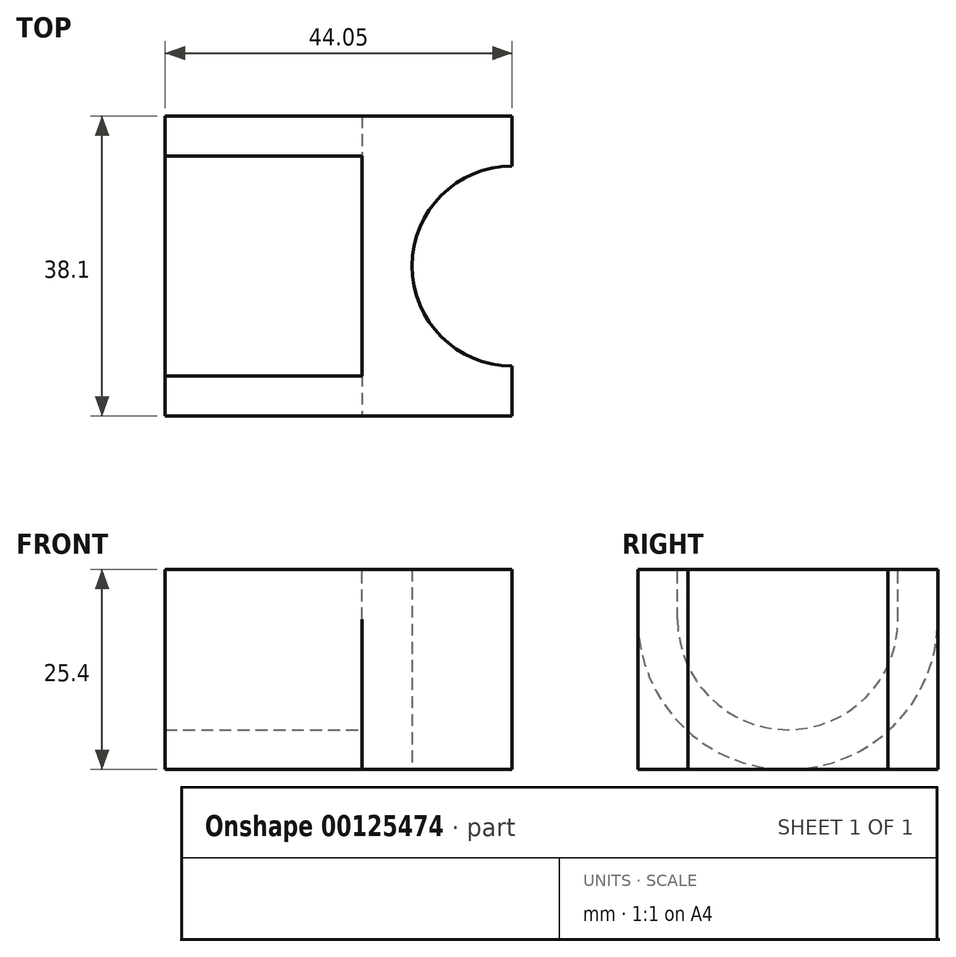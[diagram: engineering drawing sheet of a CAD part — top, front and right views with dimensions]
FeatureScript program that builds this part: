
annotation { "Feature Type Name" : "Feature", "Feature Type Description" : "" }
export const myFeature = defineFeature(function(context is Context, id is Id, definition is map)
    precondition{}
    {
        {
            var Q0;
            Q0=qCreatedBy(makeId("Top.planeOp"),FACE);
            var sketch = newSketch(context, id + "F0", { "sketchPlane" : qUnion([Q0])});
            skLineSegment(sketch, "E0.bottom", {"start": v(-6.35, 19.05) * mm, "end": v(12.7, 19.05) * mm});
            skLineSegment(sketch, "E0.top", {"start": v(-6.35, -19.05) * mm, "end": v(12.7, -19.05) * mm});
            skLineSegment(sketch, "E0.left", {"start": v(-6.35, 19.05) * mm, "end": v(-6.35, -19.05) * mm});
            skLineSegment(sketch, "E0.right", {"start": v(12.7, 19.05) * mm, "end": v(12.7, 12.7) * mm});
            skArc(sketch, "E1", {"start": v(12.7, 12.7) * mm, "mid": v(0, 0) * mm, "end": v(12.7, -12.7) * mm});
            skLineSegment(sketch, "E2.trimOffspring", {"start": v(12.7, -12.7) * mm, "end": v(12.7, -19.05) * mm});
            skSolve(sketch);
        }
        {
            var Q0;
            Q0 = qSketchRegion(id + "F0", true);
            extrude(context, id + "F1", {"entities" : qUnion([Q0]), "depth" : 25.4 * mm});
        }
        {
            var Q0;
            Q0=makeQuery(id+"F1.opExtrude","SWEPT_FACE",FACE,{"disambiguationData":[OSD([sQuery(id+"F0.wireOp",EDGE,"E0.left")])]});
            var sketch = newSketch(context, id + "F2", { "sketchPlane" : qUnion([Q0])});
            skArc(sketch, "E3", {"start": v(-19.05, 19.05) * mm, "mid": v(0, 0) * mm, "end": v(19.05, 19.05) * mm});
            skLineSegment(sketch, "E4", {"start": v(-19.05, 19.05) * mm, "end": v(19.05, 19.05) * mm, "construction": true});
            skLineSegment(sketch, "E5", {"start": v(-19.05, 19.05) * mm, "end": v(-19.05, 25.4) * mm});
            skLineSegment(sketch, "E6", {"start": v(19.05, 19.05) * mm, "end": v(19.05, 25.4) * mm});
            skArc(sketch, "E7", {"start": v(-14, 19.05) * mm, "mid": v(0, 5.05) * mm, "end": v(14, 19.05) * mm});
            skLineSegment(sketch, "E8", {"start": v(-14, 19.05) * mm, "end": v(-14, 25.4) * mm});
            skLineSegment(sketch, "E9", {"start": v(-14, 25.4) * mm, "end": v(-19.05, 25.4) * mm});
            skLineSegment(sketch, "E10", {"start": v(14, 19.05) * mm, "end": v(14, 25.4) * mm});
            skLineSegment(sketch, "E11", {"start": v(14, 25.4) * mm, "end": v(19.05, 25.4) * mm});
            skSolve(sketch);
        }
        {
            var Q0;
            Q0 = qSketchRegion(id + "F2", true);
            extrude(context, id + "F3", {"entities" : qUnion([Q0]), "operationType" : NewBodyOperationType.ADD, "depth" : 25 * mm});
        }
    });
